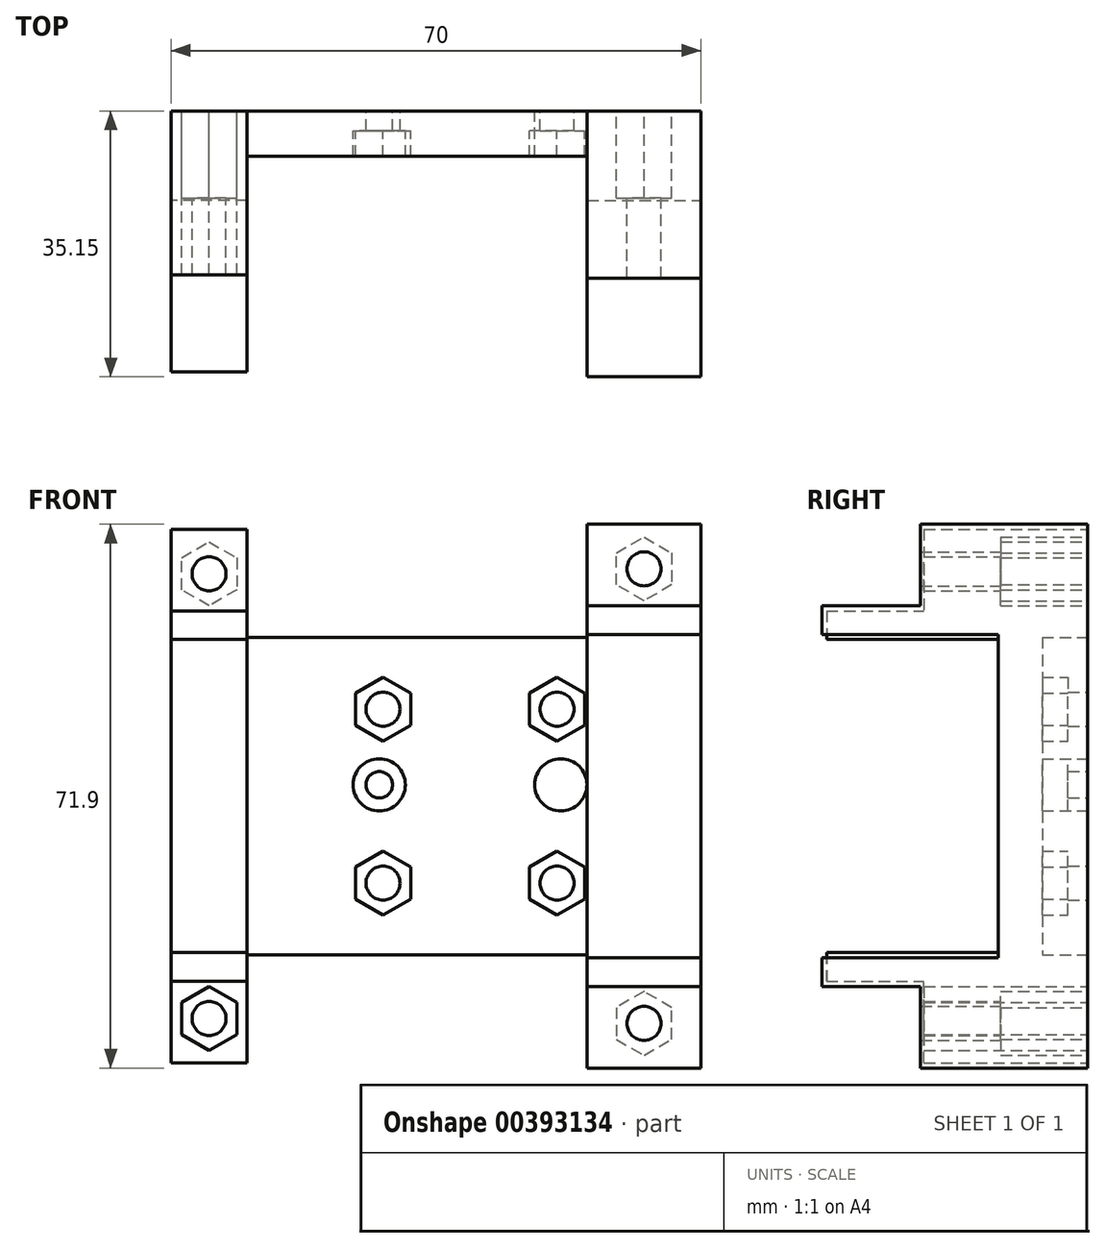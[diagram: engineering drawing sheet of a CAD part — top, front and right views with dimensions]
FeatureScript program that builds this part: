
annotation { "Feature Type Name" : "Feature", "Feature Type Description" : "" }
export const myFeature = defineFeature(function(context is Context, id is Id, definition is map)
    precondition{}
    {
        {
            var Q0;
            Q0=qCreatedBy(makeId("Front.planeOp"),FACE);
            var sketch = newSketch(context, id + "F0", { "sketchPlane" : qUnion([Q0])});
            skLineSegment(sketch, "E0", {"start": v(-39.5, 35.3) * mm, "end": v(-29.5, 35.3) * mm});
            skLineSegment(sketch, "E1", {"start": v(-29.5, 35.3) * mm, "end": v(-29.5, 21) * mm});
            skLineSegment(sketch, "E2", {"start": v(-29.5, 21) * mm, "end": v(15.5, 21) * mm});
            skLineSegment(sketch, "E3", {"start": v(15.5, 21) * mm, "end": v(15.5, 35.95) * mm});
            skLineSegment(sketch, "E4", {"start": v(15.5, 35.95) * mm, "end": v(30.5, 35.95) * mm});
            skLineSegment(sketch, "E5.MirrorCS", {"start": v(-39.5, -35.3) * mm, "end": v(-29.5, -35.3) * mm});
            skLineSegment(sketch, "E6.MirrorCS", {"start": v(-29.5, -21) * mm, "end": v(15.5, -21) * mm});
            skLineSegment(sketch, "E7.MirrorCS", {"start": v(15.5, -35.95) * mm, "end": v(30.5, -35.95) * mm});
            skLineSegment(sketch, "E8.MirrorCS", {"start": v(-29.5, -35.3) * mm, "end": v(-29.5, -21) * mm});
            skLineSegment(sketch, "E9.MirrorCS", {"start": v(15.5, -21) * mm, "end": v(15.5, -35.95) * mm});
            skLineSegment(sketch, "E10", {"start": v(-39.5, 35.3) * mm, "end": v(-39.5, -35.3) * mm});
            skLineSegment(sketch, "E11", {"start": v(30.5, 35.95) * mm, "end": v(30.5, -35.95) * mm});
            skLineSegment(sketch, "E12", {"start": v(-29.5, 21) * mm, "end": v(-29.5, -21) * mm});
            skLineSegment(sketch, "E13", {"start": v(15.5, 21) * mm, "end": v(15.5, -21) * mm});
            skPoint(sketch, "E14", {"position": v(-7, 21) * mm});
            skCircle(sketch, "E15", {"center": v(-34.5, 29.4) * mm, "radius": 2.25 * mm});
            skPoint(sketch, "E15.centerSnap0", {"position": v(-34.5, 35.3) * mm});
            skCircle(sketch, "E16.MirrorC", {"center": v(-34.5, -29.4) * mm, "radius": 2.25 * mm});
            skCircle(sketch, "E17", {"center": v(23, 30.05) * mm, "radius": 2.25 * mm});
            skPoint(sketch, "E17.centerSnap0", {"position": v(23, 35.95) * mm});
            skLineSegment(sketch, "E18", {"start": v(-39.5, 24.5) * mm, "end": v(-29.5, 24.5) * mm});
            skLineSegment(sketch, "E19", {"start": v(-29.5, 20.7) * mm, "end": v(-39.5, 20.7) * mm});
            skLineSegment(sketch, "E20", {"start": v(15.5, 21.35) * mm, "end": v(30.5, 21.35) * mm});
            skLineSegment(sketch, "E21", {"start": v(15.5, 25.15) * mm, "end": v(30.5, 25.15) * mm});
            skLineSegment(sketch, "E22.MirrorCS", {"start": v(-29.5, -20.7) * mm, "end": v(-39.5, -20.7) * mm});
            skLineSegment(sketch, "E23.MirrorCS", {"start": v(-39.5, -24.5) * mm, "end": v(-29.5, -24.5) * mm});
            skLineSegment(sketch, "E24.MirrorCS", {"start": v(15.5, -25.15) * mm, "end": v(30.5, -25.15) * mm});
            skLineSegment(sketch, "E25.MirrorCS", {"start": v(15.5, -21.35) * mm, "end": v(30.5, -21.35) * mm});
            skCircle(sketch, "E26", {"center": v(-11.5, 11.5) * mm, "radius": 2.25 * mm});
            skCircle(sketch, "E27.cCircle", {"center": v(-11.5, 11.5) * mm, "radius": 3.65 * mm, "construction": true});
            skLineSegment(sketch, "E27.0", {"start": v(-7.85, 13.6) * mm, "end": v(-7.85, 9.4) * mm});
            skLineSegment(sketch, "E27.1", {"start": v(-7.85, 9.4) * mm, "end": v(-11.5, 7.29) * mm});
            skLineSegment(sketch, "E27.2", {"start": v(-11.5, 7.29) * mm, "end": v(-15.15, 9.4) * mm});
            skLineSegment(sketch, "E27.3", {"start": v(-15.15, 9.4) * mm, "end": v(-15.15, 13.6) * mm});
            skLineSegment(sketch, "E27.4", {"start": v(-15.15, 13.6) * mm, "end": v(-11.5, 15.71) * mm});
            skLineSegment(sketch, "E27.5", {"start": v(-11.5, 15.71) * mm, "end": v(-7.85, 13.6) * mm});
            skPoint(sketch, "E27.0.midPoint", {"position": v(-7.85, 11.5) * mm});
            skLineSegment(sketch, "E28.MirrorCS", {"start": v(-15.15, -9.4) * mm, "end": v(-15.15, -13.6) * mm});
            skLineSegment(sketch, "E29.MirrorCS", {"start": v(-7.85, -13.6) * mm, "end": v(-7.85, -9.4) * mm});
            skLineSegment(sketch, "E30.MirrorCS", {"start": v(-11.5, -15.71) * mm, "end": v(-7.85, -13.6) * mm});
            skLineSegment(sketch, "E31.MirrorCS", {"start": v(-11.5, -7.29) * mm, "end": v(-15.15, -9.4) * mm});
            skCircle(sketch, "E32.MirrorC", {"center": v(-11.5, -11.5) * mm, "radius": 2.25 * mm});
            skCircle(sketch, "E33.MirrorC", {"center": v(-11.5, -11.5) * mm, "radius": 3.65 * mm, "construction": true});
            skPoint(sketch, "E34.MirrorP", {"position": v(-7.85, -11.5) * mm});
            skLineSegment(sketch, "E35.MirrorCS", {"start": v(-15.15, -13.6) * mm, "end": v(-11.5, -15.71) * mm});
            skLineSegment(sketch, "E36.MirrorCS", {"start": v(-7.85, -9.4) * mm, "end": v(-11.5, -7.29) * mm});
            skLineSegment(sketch, "E37.MirrorCS", {"start": v(7.85, -13.6) * mm, "end": v(7.85, -9.4) * mm});
            skLineSegment(sketch, "E38.MirrorCS", {"start": v(7.85, 13.6) * mm, "end": v(7.85, 9.4) * mm});
            skLineSegment(sketch, "E39.MirrorCS", {"start": v(11.5, -15.71) * mm, "end": v(7.85, -13.6) * mm});
            skLineSegment(sketch, "E40.MirrorCS", {"start": v(15.15, -13.6) * mm, "end": v(11.5, -15.71) * mm});
            skLineSegment(sketch, "E41.MirrorCS", {"start": v(15.15, -9.4) * mm, "end": v(15.15, -13.6) * mm});
            skLineSegment(sketch, "E42.MirrorCS", {"start": v(15.15, 9.4) * mm, "end": v(15.15, 13.6) * mm});
            skCircle(sketch, "E43.MirrorC", {"center": v(11.5, -11.5) * mm, "radius": 2.25 * mm});
            skLineSegment(sketch, "E44.MirrorCS", {"start": v(7.85, -9.4) * mm, "end": v(11.5, -7.29) * mm});
            skLineSegment(sketch, "E45.MirrorCS", {"start": v(11.5, 15.71) * mm, "end": v(7.85, 13.6) * mm});
            skCircle(sketch, "E46.MirrorC", {"center": v(11.5, 11.5) * mm, "radius": 2.25 * mm});
            skPoint(sketch, "E47.MirrorP", {"position": v(7, 21) * mm});
            skLineSegment(sketch, "E48.MirrorCS", {"start": v(15.15, 13.6) * mm, "end": v(11.5, 15.71) * mm});
            skLineSegment(sketch, "E49.MirrorCS", {"start": v(7.85, 9.4) * mm, "end": v(11.5, 7.29) * mm});
            skPoint(sketch, "E50.MirrorP", {"position": v(7.85, -11.5) * mm});
            skCircle(sketch, "E51.MirrorC", {"center": v(11.5, -11.5) * mm, "radius": 3.65 * mm, "construction": true});
            skPoint(sketch, "E52.MirrorP", {"position": v(7.85, 11.5) * mm});
            skLineSegment(sketch, "E53.MirrorCS", {"start": v(11.5, 7.29) * mm, "end": v(15.15, 9.4) * mm});
            skLineSegment(sketch, "E54.MirrorCS", {"start": v(11.5, -7.29) * mm, "end": v(15.15, -9.4) * mm});
            skCircle(sketch, "E55.MirrorC", {"center": v(11.5, 11.5) * mm, "radius": 3.65 * mm, "construction": true});
            skCircle(sketch, "E56.cCircle", {"center": v(-34.5, 29.4) * mm, "radius": 3.65 * mm, "construction": true});
            skLineSegment(sketch, "E56.0", {"start": v(-30.85, 31.5) * mm, "end": v(-30.85, 27.3) * mm});
            skLineSegment(sketch, "E56.1", {"start": v(-30.85, 27.3) * mm, "end": v(-34.5, 25.19) * mm});
            skLineSegment(sketch, "E56.2", {"start": v(-34.5, 25.19) * mm, "end": v(-38.15, 27.3) * mm});
            skLineSegment(sketch, "E56.3", {"start": v(-38.15, 27.3) * mm, "end": v(-38.15, 31.5) * mm});
            skLineSegment(sketch, "E56.4", {"start": v(-38.15, 31.5) * mm, "end": v(-34.5, 33.61) * mm});
            skLineSegment(sketch, "E56.5", {"start": v(-34.5, 33.61) * mm, "end": v(-30.85, 31.5) * mm});
            skPoint(sketch, "E56.0.midPoint", {"position": v(-30.85, 29.4) * mm});
            skCircle(sketch, "E57.cCircle", {"center": v(-34.5, -29.4) * mm, "radius": 3.65 * mm, "construction": true});
            skLineSegment(sketch, "E57.0", {"start": v(-30.85, -27.3) * mm, "end": v(-30.85, -31.5) * mm});
            skLineSegment(sketch, "E57.1", {"start": v(-30.85, -31.5) * mm, "end": v(-34.5, -33.61) * mm});
            skLineSegment(sketch, "E57.2", {"start": v(-34.5, -33.61) * mm, "end": v(-38.15, -31.5) * mm});
            skLineSegment(sketch, "E57.3", {"start": v(-38.15, -31.5) * mm, "end": v(-38.15, -27.3) * mm});
            skLineSegment(sketch, "E57.4", {"start": v(-38.15, -27.3) * mm, "end": v(-34.5, -25.19) * mm});
            skLineSegment(sketch, "E57.5", {"start": v(-34.5, -25.19) * mm, "end": v(-30.85, -27.3) * mm});
            skPoint(sketch, "E57.0.midPoint", {"position": v(-30.85, -29.4) * mm});
            skCircle(sketch, "E58.cCircle", {"center": v(23, 30.05) * mm, "radius": 3.65 * mm, "construction": true});
            skLineSegment(sketch, "E58.0", {"start": v(26.65, 32.16) * mm, "end": v(26.65, 27.94) * mm});
            skLineSegment(sketch, "E58.1", {"start": v(26.65, 27.94) * mm, "end": v(23, 25.84) * mm});
            skLineSegment(sketch, "E58.2", {"start": v(23, 25.84) * mm, "end": v(19.35, 27.94) * mm});
            skLineSegment(sketch, "E58.3", {"start": v(19.35, 27.94) * mm, "end": v(19.35, 32.16) * mm});
            skLineSegment(sketch, "E58.4", {"start": v(19.35, 32.16) * mm, "end": v(23, 34.26) * mm});
            skLineSegment(sketch, "E58.5", {"start": v(23, 34.26) * mm, "end": v(26.65, 32.16) * mm});
            skPoint(sketch, "E58.0.midPoint", {"position": v(26.65, 30.05) * mm});
            skLineSegment(sketch, "E59.MirrorCS", {"start": v(26.65, -32.16) * mm, "end": v(26.65, -27.94) * mm});
            skPoint(sketch, "E60.MirrorP", {"position": v(23, -35.95) * mm});
            skPoint(sketch, "E61.MirrorP", {"position": v(26.65, -30.05) * mm});
            skLineSegment(sketch, "E62.MirrorCS", {"start": v(23, -25.84) * mm, "end": v(19.35, -27.94) * mm});
            skLineSegment(sketch, "E63.MirrorCS", {"start": v(19.35, -27.94) * mm, "end": v(19.35, -32.16) * mm});
            skLineSegment(sketch, "E64.MirrorCS", {"start": v(23, -34.26) * mm, "end": v(26.65, -32.16) * mm});
            skLineSegment(sketch, "E65.MirrorCS", {"start": v(19.35, -32.16) * mm, "end": v(23, -34.26) * mm});
            skLineSegment(sketch, "E66.MirrorCS", {"start": v(26.65, -27.94) * mm, "end": v(23, -25.84) * mm});
            skCircle(sketch, "E67.MirrorC", {"center": v(23, -30.05) * mm, "radius": 2.25 * mm});
            skCircle(sketch, "E68.MirrorC", {"center": v(23, -30.05) * mm, "radius": 3.65 * mm, "construction": true});
            skCircle(sketch, "E69", {"center": v(-12, 1.5) * mm, "radius": 1.75 * mm});
            skCircle(sketch, "E70", {"center": v(-12, 1.5) * mm, "radius": 3.45 * mm});
            skCircle(sketch, "E71.MirrorC", {"center": v(12, 1.5) * mm, "radius": 3.45 * mm});
            skCircle(sketch, "E72.MirrorC", {"center": v(12, 1.5) * mm, "radius": 1.75 * mm});
            skSolve(sketch);
        }
        {
            var Q0;
            {var subQ1=sQuery(id+"F0.wireOp",EDGE,"E2");Q0=makeQuery(id+"F0.imprint","IMPRINT",FACE,{"disambiguationData":[TD([[makeQuery(id+"F0.imprint","IMPRINT",EDGE,{"derivedFrom":subQ1}),-1.0]])]});}
            extrude(context, id + "F1", {"entities" : qUnion([Q0]), "depth" : 6 * mm});
        }
        {
            var Q0;
            {var subQ0=sQuery(id+"F0.wireOp",EDGE,"E19");Q0=makeQuery(id+"F0.imprint","IMPRINT",FACE,{"disambiguationData":[TD([[makeQuery(id+"F0.imprint","IMPRINT",EDGE,{"derivedFrom":subQ0}),1.0]])]});}
            var Q1;
            {var subQ3=sQuery(id+"F0.wireOp",EDGE,"E13");Q1=makeQuery(id+"F0.imprint","IMPRINT",FACE,{"disambiguationData":[TD([[makeQuery(id+"F0.imprint","IMPRINT",EDGE,{"derivedFrom":subQ3}),1.0]])]});}
            extrude(context, id + "F2", {"entities" : qUnion([Q0, Q1]), "operationType" : NewBodyOperationType.ADD, "depth" : 11.8 * mm});
        }
        {
            var Q0;
            {var subQ0=sQuery(id+"F0.wireOp",EDGE,"E18");Q0=makeQuery(id+"F0.imprint","IMPRINT",FACE,{"disambiguationData":[TD([[makeQuery(id+"F0.imprint","IMPRINT",EDGE,{"derivedFrom":subQ0}),-1.0]])]});}
            var Q1;
            {var subQ3=sQuery(id+"F0.wireOp",EDGE,"E22.MirrorCS");Q1=makeQuery(id+"F0.imprint","IMPRINT",FACE,{"disambiguationData":[TD([[makeQuery(id+"F0.imprint","IMPRINT",EDGE,{"derivedFrom":subQ3}),1.0]])]});}
            extrude(context, id + "F3", {"entities" : qUnion([Q0, Q1]), "operationType" : NewBodyOperationType.ADD, "depth" : 34.5 * mm});
        }
        {
            var Q0;
            {var subQ0=sQuery(id+"F0.wireOp",EDGE,"E24.MirrorCS");Q0=makeQuery(id+"F0.imprint","IMPRINT",FACE,{"disambiguationData":[TD([[makeQuery(id+"F0.imprint","IMPRINT",EDGE,{"derivedFrom":subQ0}),1.0]])]});}
            var Q1;
            {var subQ0=sQuery(id+"F0.wireOp",EDGE,"E20");Q1=makeQuery(id+"F0.imprint","IMPRINT",FACE,{"disambiguationData":[TD([[makeQuery(id+"F0.imprint","IMPRINT",EDGE,{"derivedFrom":subQ0}),1.0]])]});}
            extrude(context, id + "F4", {"entities" : qUnion([Q0, Q1]), "operationType" : NewBodyOperationType.ADD, "depth" : 35.15 * mm});
        }
        {
            var Q0;
            {var subQ1=sQuery(id+"F0.wireOp",EDGE,"E5.MirrorCS");Q0=makeQuery(id+"F0.imprint","IMPRINT",FACE,{"disambiguationData":[TD([[makeQuery(id+"F0.imprint","IMPRINT",EDGE,{"derivedFrom":subQ1}),1.0]])]});}
            var Q1;
            Q1=makeQuery(id+"F0.imprint","IMPRINT",FACE,{"disambiguationData":[TD([[makeQuery(id+"F0.imprint","IMPRINT",EDGE,{"derivedFrom":sQuery(id+"F0.wireOp",EDGE,"E16.MirrorC")}),1.0]])]});
            var Q2;
            {var subQ1=sQuery(id+"F0.wireOp",EDGE,"E0");Q2=makeQuery(id+"F0.imprint","IMPRINT",FACE,{"disambiguationData":[TD([[makeQuery(id+"F0.imprint","IMPRINT",EDGE,{"derivedFrom":subQ1}),-1.0]])]});}
            var Q3;
            Q3=makeQuery(id+"F0.imprint","IMPRINT",FACE,{"disambiguationData":[TD([[makeQuery(id+"F0.imprint","IMPRINT",EDGE,{"derivedFrom":sQuery(id+"F0.wireOp",EDGE,"E15")}),-1.0]])]});
            extrude(context, id + "F5", {"entities" : qUnion([Q0, Q1, Q2, Q3]), "operationType" : NewBodyOperationType.ADD, "depth" : 21.67 * mm});
        }
        {
            var Q0;
            {var subQ2=sQuery(id+"F0.wireOp",EDGE,"E7.MirrorCS");Q0=makeQuery(id+"F0.imprint","IMPRINT",FACE,{"disambiguationData":[TD([[makeQuery(id+"F0.imprint","IMPRINT",EDGE,{"derivedFrom":subQ2}),1.0]])]});}
            var Q1;
            Q1=makeQuery(id+"F0.imprint","IMPRINT",FACE,{"disambiguationData":[TD([[makeQuery(id+"F0.imprint","IMPRINT",EDGE,{"derivedFrom":sQuery(id+"F0.wireOp",EDGE,"E59.MirrorCS")}),1.0]])]});
            var Q2;
            {var subQ0=sQuery(id+"F0.wireOp",EDGE,"E4");Q2=makeQuery(id+"F0.imprint","IMPRINT",FACE,{"disambiguationData":[TD([[makeQuery(id+"F0.imprint","IMPRINT",EDGE,{"derivedFrom":subQ0}),-1.0]])]});}
            var Q3;
            Q3=makeQuery(id+"F0.imprint","IMPRINT",FACE,{"disambiguationData":[TD([[makeQuery(id+"F0.imprint","IMPRINT",EDGE,{"derivedFrom":sQuery(id+"F0.wireOp",EDGE,"E17")}),-1.0]])]});
            extrude(context, id + "F6", {"entities" : qUnion([Q0, Q1, Q2, Q3]), "operationType" : NewBodyOperationType.ADD, "depth" : 22.1 * mm});
        }
        {
            var Q0;
            Q0=makeQuery(id+"F0.imprint","IMPRINT",FACE,{"disambiguationData":[TD([[makeQuery(id+"F0.imprint","IMPRINT",EDGE,{"derivedFrom":sQuery(id+"F0.wireOp",EDGE,"E26")}),-1.0]])]});
            var Q1;
            Q1=makeQuery(id+"F0.imprint","IMPRINT",FACE,{"disambiguationData":[TD([[makeQuery(id+"F0.imprint","IMPRINT",EDGE,{"derivedFrom":sQuery(id+"F0.wireOp",EDGE,"E38.MirrorCS")}),1.0]])]});
            var Q2;
            Q2=makeQuery(id+"F0.imprint","IMPRINT",FACE,{"disambiguationData":[TD([[makeQuery(id+"F0.imprint","IMPRINT",EDGE,{"derivedFrom":sQuery(id+"F0.wireOp",EDGE,"E37.MirrorCS")}),-1.0]])]});
            var Q3;
            Q3=makeQuery(id+"F0.imprint","IMPRINT",FACE,{"disambiguationData":[TD([[makeQuery(id+"F0.imprint","IMPRINT",EDGE,{"derivedFrom":sQuery(id+"F0.wireOp",EDGE,"E28.MirrorCS")}),1.0]])]});
            var Q4;
            Q4=makeQuery(id+"F0.imprint","IMPRINT",FACE,{"disambiguationData":[TD([[makeQuery(id+"F0.imprint","IMPRINT",EDGE,{"derivedFrom":sQuery(id+"F0.wireOp",EDGE,"E69")}),-1.0]])]});
            var Q5;
            Q5=makeQuery(id+"F0.imprint","IMPRINT",FACE,{"disambiguationData":[TD([[makeQuery(id+"F0.imprint","IMPRINT",EDGE,{"derivedFrom":sQuery(id+"F0.wireOp",EDGE,"E71.MirrorC")}),-1.0]])]});
            extrude(context, id + "F7", {"entities" : qUnion([Q0, Q1, Q2, Q3, Q4, Q5]), "operationType" : NewBodyOperationType.ADD, "depth" : 2.6 * mm});
        }
        {
            var Q0;
            Q0=makeQuery(id+"F0.imprint","IMPRINT",FACE,{"disambiguationData":[TD([[makeQuery(id+"F0.imprint","IMPRINT",EDGE,{"derivedFrom":sQuery(id+"F0.wireOp",EDGE,"E59.MirrorCS")}),1.0]])]});
            var Q1;
            Q1=makeQuery(id+"F0.imprint","IMPRINT",FACE,{"disambiguationData":[TD([[makeQuery(id+"F0.imprint","IMPRINT",EDGE,{"derivedFrom":sQuery(id+"F0.wireOp",EDGE,"E17")}),-1.0]])]});
            var Q2;
            Q2=makeQuery(id+"F0.imprint","IMPRINT",FACE,{"disambiguationData":[TD([[makeQuery(id+"F0.imprint","IMPRINT",EDGE,{"derivedFrom":sQuery(id+"F0.wireOp",EDGE,"E15")}),-1.0]])]});
            var Q3;
            Q3=makeQuery(id+"F0.imprint","IMPRINT",FACE,{"disambiguationData":[TD([[makeQuery(id+"F0.imprint","IMPRINT",EDGE,{"derivedFrom":sQuery(id+"F0.wireOp",EDGE,"E16.MirrorC")}),1.0]])]});
            extrude(context, id + "F8", {"entities" : qUnion([Q0, Q1, Q2, Q3]), "operationType" : NewBodyOperationType.REMOVE, "depth" : 11.5 * mm});
        }
    });
